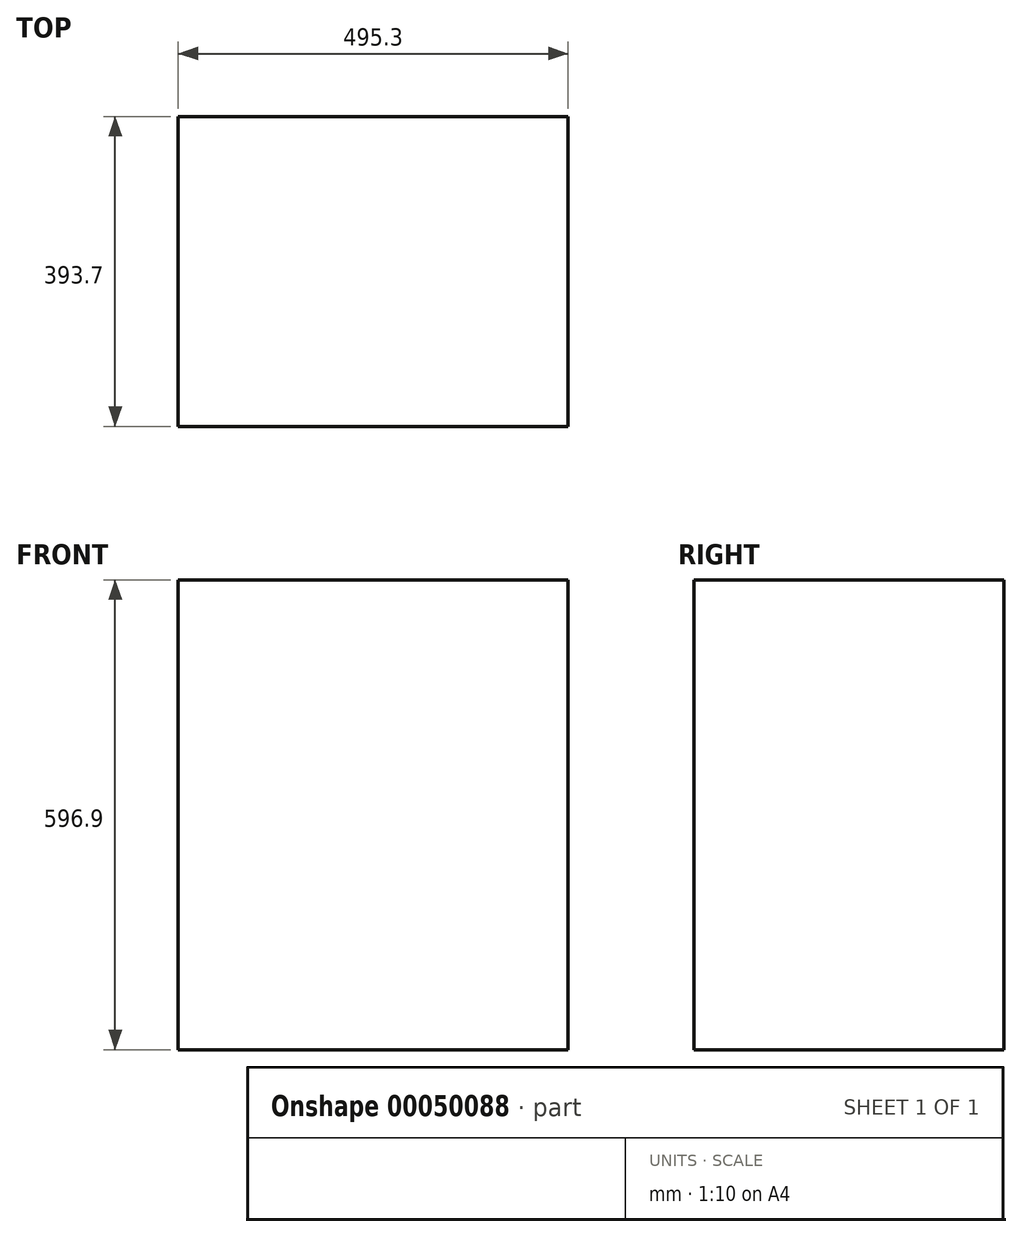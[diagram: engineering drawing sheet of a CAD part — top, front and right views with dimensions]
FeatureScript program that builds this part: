
annotation { "Feature Type Name" : "Feature", "Feature Type Description" : "" }
export const myFeature = defineFeature(function(context is Context, id is Id, definition is map)
    precondition{}
    {
        {
            var Q0;
            Q0=qCreatedBy(makeId("Top.planeOp"),FACE);
            var sketch = newSketch(context, id + "F0", { "sketchPlane" : qUnion([Q0])});
            skLineSegment(sketch, "E0.bottom", {"start": v(-247.65, 196.85) * mm, "end": v(247.65, 196.85) * mm});
            skLineSegment(sketch, "E0.top", {"start": v(-247.65, -196.85) * mm, "end": v(247.65, -196.85) * mm});
            skLineSegment(sketch, "E0.left", {"start": v(-247.65, 196.85) * mm, "end": v(-247.65, -196.85) * mm});
            skLineSegment(sketch, "E0.right", {"start": v(247.65, 196.85) * mm, "end": v(247.65, -196.85) * mm});
            skSolve(sketch);
        }
        {
            var Q0;
            Q0 = qSketchRegion(id + "F0", true);
            extrude(context, id + "F1", {"entities" : qUnion([Q0]), "depth" : 596.9 * mm});
        }
    });
